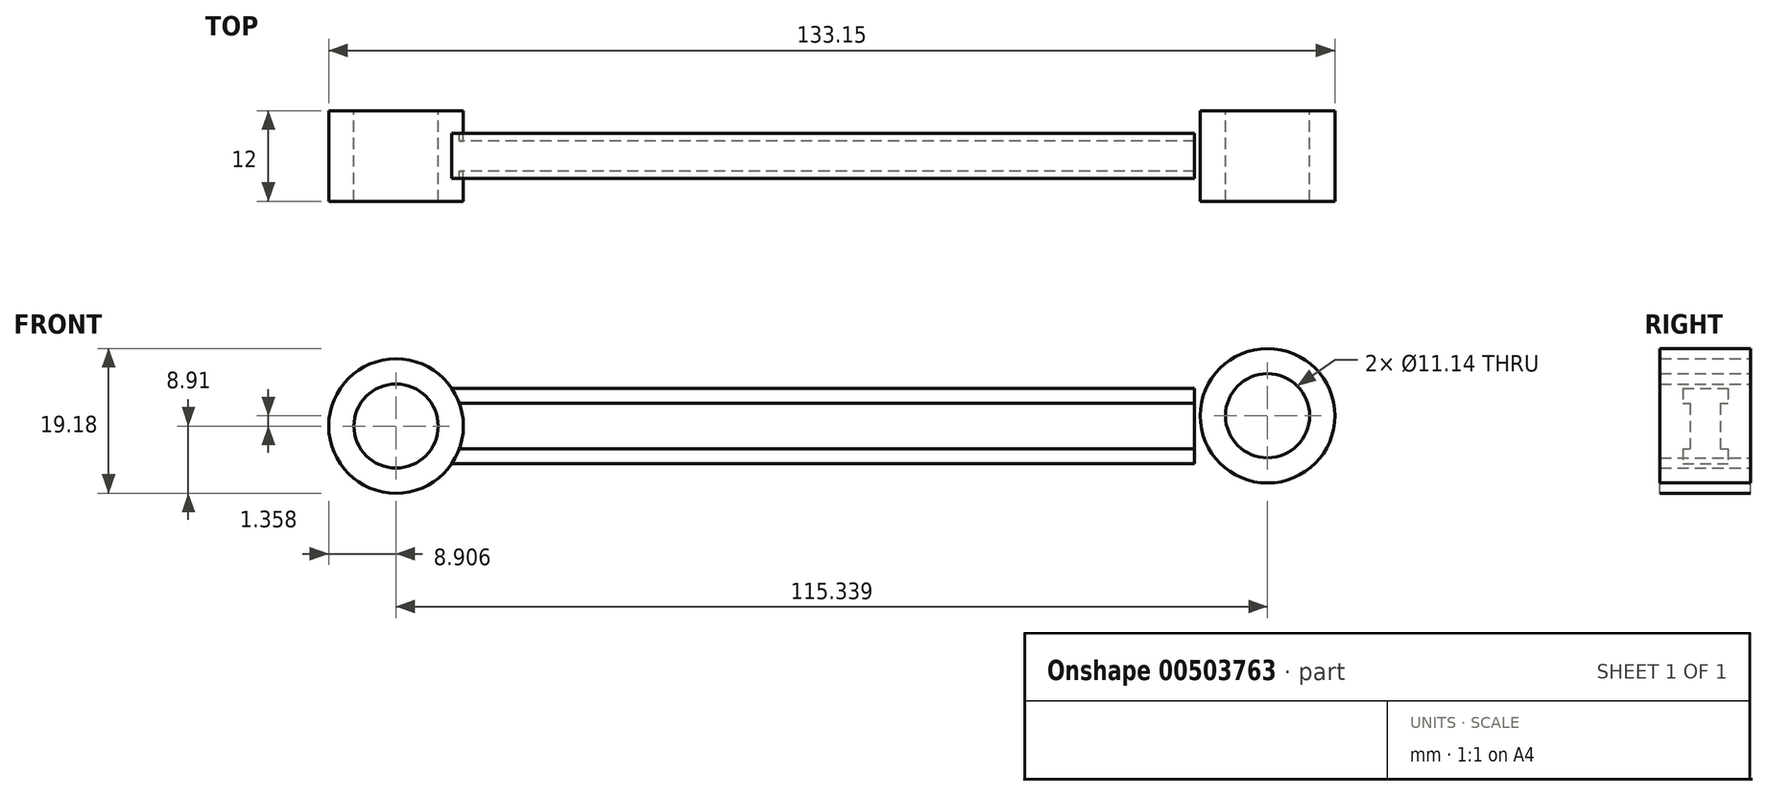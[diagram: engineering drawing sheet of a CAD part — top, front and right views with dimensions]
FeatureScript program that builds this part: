
annotation { "Feature Type Name" : "Feature", "Feature Type Description" : "" }
export const myFeature = defineFeature(function(context is Context, id is Id, definition is map)
    precondition{}
    {
        {
            var Q0;
            Q0=qCreatedBy(makeId("Right.planeOp"),FACE);
            var sketch = newSketch(context, id + "F0", { "sketchPlane" : qUnion([Q0])});
            skLineSegment(sketch, "E0.bottom", {"start": v(-3, 5) * mm, "end": v(3, 5) * mm});
            skLineSegment(sketch, "E0.top", {"start": v(-3, 3) * mm, "end": v(3, 3) * mm});
            skLineSegment(sketch, "E0.left", {"start": v(-3, 5) * mm, "end": v(-3, 3) * mm});
            skLineSegment(sketch, "E0.right", {"start": v(3, 5) * mm, "end": v(3, 3) * mm});
            skLineSegment(sketch, "E1.bottom", {"start": v(-3, -3) * mm, "end": v(3, -3) * mm});
            skLineSegment(sketch, "E1.top", {"start": v(-3, -5) * mm, "end": v(3, -5) * mm});
            skLineSegment(sketch, "E1.left", {"start": v(-3, -3) * mm, "end": v(-3, -5) * mm});
            skLineSegment(sketch, "E1.right", {"start": v(3, -3) * mm, "end": v(3, -5) * mm});
            skLineSegment(sketch, "E2.left", {"start": v(-2, 3) * mm, "end": v(-2, -3) * mm});
            skLineSegment(sketch, "E2.right", {"start": v(2, 3) * mm, "end": v(2, -3) * mm});
            skLineSegment(sketch, "E3", {"start": v(-3, 3) * mm, "end": v(-2, 3) * mm});
            skLineSegment(sketch, "E4", {"start": v(2, 3) * mm, "end": v(3, 3) * mm});
            skLineSegment(sketch, "E5", {"start": v(3, -3) * mm, "end": v(2, -3) * mm});
            skLineSegment(sketch, "E6", {"start": v(-2, -3) * mm, "end": v(-3, -3) * mm});
            skLineSegment(sketch, "E7", {"start": v(-3, 5) * mm, "end": v(0, 5) * mm});
            skLineSegment(sketch, "E8", {"start": v(0, 5) * mm, "end": v(3, 5) * mm});
            skLineSegment(sketch, "E9", {"start": v(-3, -5) * mm, "end": v(0, -5) * mm});
            skLineSegment(sketch, "E10", {"start": v(0, -5) * mm, "end": v(3, -5) * mm});
            skLineSegment(sketch, "E11", {"start": v(-3, -3) * mm, "end": v(-2, -3) * mm});
            skLineSegment(sketch, "E12", {"start": v(0, 3) * mm, "end": v(0, 0) * mm});
            skLineSegment(sketch, "E13", {"start": v(0, 0) * mm, "end": v(0, -3) * mm});
            skSolve(sketch);
        }
        {
            var Q0;
            Q0=makeQuery(id+"F0.imprint","IMPRINT",FACE,{"disambiguationData":[TD([[makeQuery(id+"F0.imprint","IMPRINT",EDGE,{"derivedFrom":sQuery(id+"F0.wireOp",EDGE,"E1.bottom")}),-1.0]])]});
            var Q1;
            Q1=makeQuery(id+"F0.imprint","IMPRINT",FACE,{"disambiguationData":[TD([[makeQuery(id+"F0.imprint","IMPRINT",EDGE,{"derivedFrom":sQuery(id+"F0.wireOp",EDGE,"E0.top")}),-1.0]])]});
            var Q2;
            Q2=makeQuery(id+"F0.imprint","IMPRINT",FACE,{"disambiguationData":[TD([[makeQuery(id+"F0.imprint","IMPRINT",EDGE,{"derivedFrom":sQuery(id+"F0.wireOp",EDGE,"E0.top")}),1.0]])]});
            extrude(context, id + "F1", {"entities" : qUnion([Q0, Q1, Q2]), "endBound" : BoundingType.SYMMETRIC, "depth" : 100 * mm});
        }
        {
            var Q0;
            Q0=qCreatedBy(makeId("Front.planeOp"),FACE);
            var sketch = newSketch(context, id + "F2", { "sketchPlane" : qUnion([Q0])});
            skPoint(sketch, "E14", {"position": v(-50.11, 0) * mm});
            skPoint(sketch, "E15", {"position": v(-55.68, 0) * mm});
            skCircle(sketch, "E16", {"center": v(-55.68, 0) * mm, "radius": 5.57 * mm});
            skCircle(sketch, "E17", {"center": v(-55.68, 0) * mm, "radius": 8.9 * mm});
            skPoint(sketch, "E18", {"position": v(65.23, 1.36) * mm});
            skPoint(sketch, "E19", {"position": v(59.66, 1.36) * mm});
            skCircle(sketch, "E20", {"center": v(59.66, 1.36) * mm, "radius": 5.57 * mm});
            skCircle(sketch, "E21", {"center": v(59.66, 1.36) * mm, "radius": 8.9 * mm});
            skSolve(sketch);
        }
        {
            var Q0;
            Q0=makeQuery(id+"F2.imprint","IMPRINT",FACE,{"disambiguationData":[TD([[makeQuery(id+"F2.imprint","IMPRINT",EDGE,{"derivedFrom":sQuery(id+"F2.wireOp",EDGE,"E16")}),-1.0]])]});
            var Q1;
            Q1=makeQuery(id+"F2.imprint","IMPRINT",FACE,{"disambiguationData":[TD([[makeQuery(id+"F2.imprint","IMPRINT",EDGE,{"derivedFrom":sQuery(id+"F2.wireOp",EDGE,"E20")}),-1.0]])]});
            extrude(context, id + "F3", {"entities" : qUnion([Q0, Q1]), "operationType" : NewBodyOperationType.ADD, "endBound" : BoundingType.SYMMETRIC, "depth" : 12 * mm});
        }
    });
